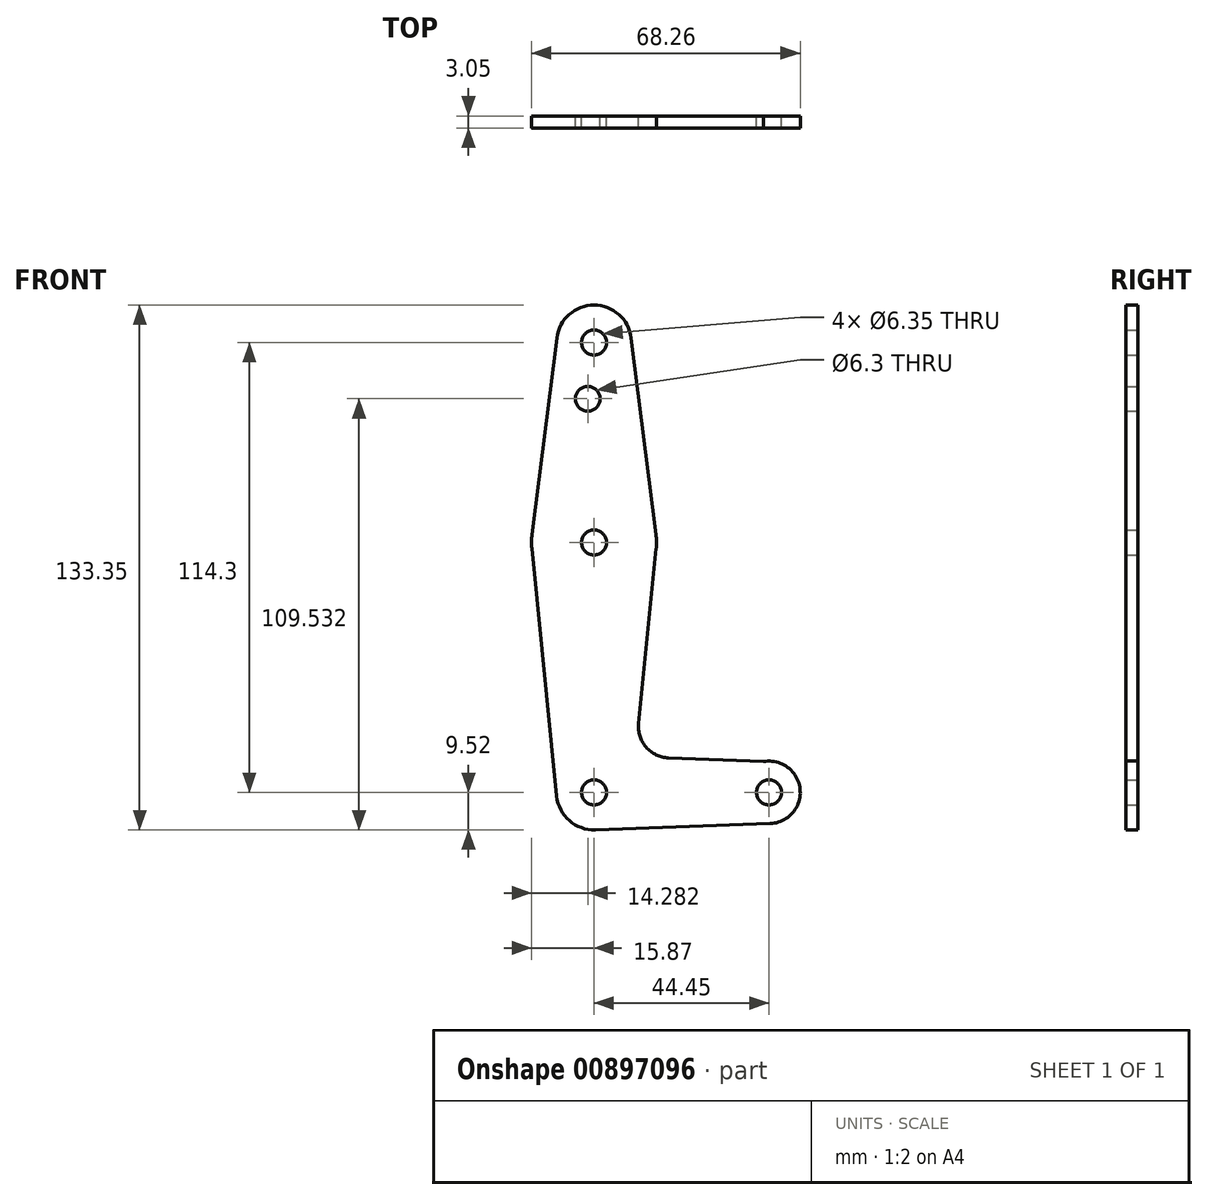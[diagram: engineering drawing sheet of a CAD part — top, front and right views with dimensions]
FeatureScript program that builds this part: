
annotation { "Feature Type Name" : "Feature", "Feature Type Description" : "" }
export const myFeature = defineFeature(function(context is Context, id is Id, definition is map)
    precondition{}
    {
        {
            var Q0;
            Q0=qCreatedBy(makeId("Front.planeOp"),FACE);
            var sketch = newSketch(context, id + "F0", { "sketchPlane" : qUnion([Q0])});
            skLineSegment(sketch, "E0", {"start": v(0, 114.3) * mm, "end": v(0, 0) * mm, "construction": true});
            skLineSegment(sketch, "E1", {"start": v(0, 0) * mm, "end": v(44.45, 0) * mm, "construction": true});
            skCircle(sketch, "E2", {"center": v(0, 114.3) * mm, "radius": 9.53 * mm});
            skCircle(sketch, "E3", {"center": v(0, 63.5) * mm, "radius": 15.88 * mm});
            skCircle(sketch, "E4", {"center": v(0, 0) * mm, "radius": 9.53 * mm});
            skCircle(sketch, "E5", {"center": v(44.45, 0) * mm, "radius": 7.94 * mm});
            skLineSegment(sketch, "E6", {"start": v(-9.45, 115.5) * mm, "end": v(-15.75, 65.48) * mm});
            skLineSegment(sketch, "E7", {"start": v(-15.8, 61.91) * mm, "end": v(-9.48, -0.95) * mm});
            skLineSegment(sketch, "E8", {"start": v(0.34, -9.52) * mm, "end": v(44.73, -7.93) * mm});
            skLineSegment(sketch, "E9", {"start": v(43.05, 7.81) * mm, "end": v(18.91, 8.78) * mm});
            skLineSegment(sketch, "E10", {"start": v(11.33, 17.5) * mm, "end": v(15.8, 61.91) * mm});
            skLineSegment(sketch, "E11", {"start": v(9.45, 115.5) * mm, "end": v(15.75, 65.48) * mm});
            skCircle(sketch, "E12", {"center": v(0, 114.3) * mm, "radius": 3.18 * mm});
            skCircle(sketch, "E13", {"center": v(0, 63.5) * mm, "radius": 3.18 * mm});
            skCircle(sketch, "E14", {"center": v(0, 0) * mm, "radius": 3.18 * mm});
            skCircle(sketch, "E15", {"center": v(44.45, 0) * mm, "radius": 3.18 * mm});
            skArc(sketch, "E16.filletArc", {"start": v(11.33, 17.5) * mm, "mid": v(13.24, 11.5) * mm, "end": v(18.91, 8.78) * mm});
            skCircle(sketch, "E17", {"center": v(-1.59, 100.01) * mm, "radius": 3.15 * mm});
            skSolve(sketch);
        }
        {
            var Q0;
            {var subQ1=sQuery(id+"F0.wireOp",EDGE,"E6");Q0=makeQuery(id+"F0.imprint","IMPRINT",FACE,{"disambiguationData":[TD([[makeQuery(id+"F0.imprint","IMPRINT",EDGE,{"derivedFrom":subQ1}),1.0]])]});}
            var Q1;
            Q1=makeQuery(id+"F0.imprint","IMPRINT",FACE,{"disambiguationData":[TD([[makeQuery(id+"F0.imprint","IMPRINT",EDGE,{"derivedFrom":sQuery(id+"F0.wireOp",EDGE,"E15")}),-1.0]])]});
            var Q2;
            {var subQ0=sQuery(id+"F0.wireOp",EDGE,"E7");Q2=makeQuery(id+"F0.imprint","IMPRINT",FACE,{"disambiguationData":[TD([[makeQuery(id+"F0.imprint","IMPRINT",EDGE,{"derivedFrom":subQ0}),1.0]])]});}
            var Q3;
            Q3=makeQuery(id+"F0.imprint","IMPRINT",FACE,{"disambiguationData":[TD([[makeQuery(id+"F0.imprint","IMPRINT",EDGE,{"derivedFrom":sQuery(id+"F0.wireOp",EDGE,"E12")}),-1.0]])]});
            var Q4;
            Q4=makeQuery(id+"F0.imprint","IMPRINT",FACE,{"disambiguationData":[TD([[makeQuery(id+"F0.imprint","IMPRINT",EDGE,{"derivedFrom":sQuery(id+"F0.wireOp",EDGE,"E13")}),-1.0]])]});
            var Q5;
            Q5=makeQuery(id+"F0.imprint","IMPRINT",FACE,{"disambiguationData":[TD([[makeQuery(id+"F0.imprint","IMPRINT",EDGE,{"derivedFrom":sQuery(id+"F0.wireOp",EDGE,"E14")}),-1.0]])]});
            extrude(context, id + "F1", {"entities" : qUnion([Q0, Q1, Q2, Q3, Q4, Q5]), "depth" : 3.05 * mm, "offsetDistance" : 25.4 * mm});
        }
    });
